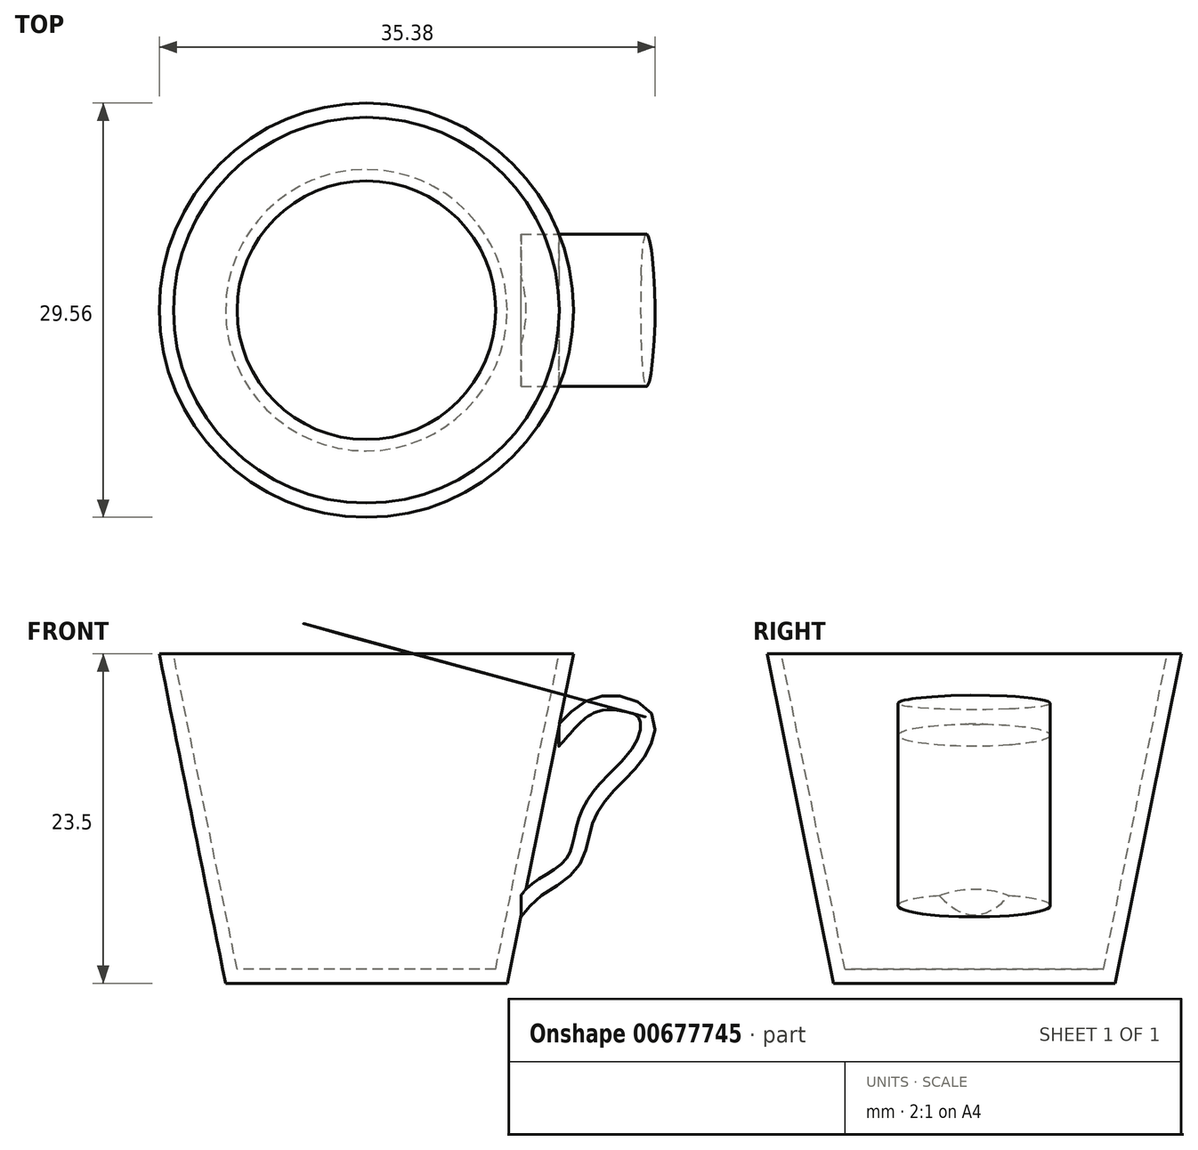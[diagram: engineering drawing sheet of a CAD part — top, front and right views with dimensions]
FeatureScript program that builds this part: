
annotation { "Feature Type Name" : "Feature", "Feature Type Description" : "" }
export const myFeature = defineFeature(function(context is Context, id is Id, definition is map)
    precondition{}
    {
        {
            var Q0;
            Q0=qCreatedBy(makeId("Front.planeOp"),FACE);
            var sketch = newSketch(context, id + "F0", { "sketchPlane" : qUnion([Q0])});
            skLineSegment(sketch, "E0", {"start": v(45.77, 48.7) * mm, "end": v(60.56, 48.7) * mm});
            skLineSegment(sketch, "E1", {"start": v(60.56, 48.7) * mm, "end": v(55.82, 25.2) * mm});
            skLineSegment(sketch, "E2", {"start": v(55.82, 25.2) * mm, "end": v(45.77, 25.2) * mm});
            skLineSegment(sketch, "E3", {"start": v(45.77, 25.2) * mm, "end": v(45.77, 48.7) * mm});
            skPoint(sketch, "E4.5.internal.snap0", {"position": v(58.19, 36.96) * mm});
            skPoint(sketch, "E4.7.internal.snap0", {"position": v(58.19, 36.96) * mm});
            skFitSpline(sketch, "E4", {"points": [v(59.42, 43.06) * mm, v(62.45, 45.3) * mm, v(65.67, 44.35) * mm, v(65.48, 41.89) * mm, v(63.4, 39.42) * mm, v(61.7, 36.96) * mm, v(60.56, 33.74) * mm, v(58.19, 31.84) * mm, v(56.9, 30.6) * mm], "startDerivative": vector(19.06, 21.07) * mm, "endDerivative": vector(-11.26, -12.92) * mm});
            skSolve(sketch);
        }
        {
            var Q0;
            Q0=makeQuery(id+"F0.imprint","IMPRINT",FACE,{"disambiguationData":[TD([[makeQuery(id+"F0.imprint","IMPRINT",EDGE,{"derivedFrom":sQuery(id+"F0.wireOp",EDGE,"E0")}),-1.0]])]});
            var Q1;
            Q1=sQuery(id+"F0.wireOp",EDGE,"E3");
            revolve(context, id + "F1", {"entities" : qUnion([Q0]), "axis" : qUnion([Q1]), "revolveType" : RevolveType.FULL});
        }
        {
            var Q0;
            Q0=makeQuery(id+"F1.opRevolve","SWEPT_FACE",FACE,{"disambiguationData":[OSD([sQuery(id+"F0.wireOp",EDGE,"E0")])]});
            shell(context, id + "F2", {"entities" : qUnion([Q0]), "thickness" : 1 * mm});
        }
        {
            var Q0;
            Q0=qCreatedBy(makeId("Right.planeOp"),FACE);
            cPlane(context, id + "F3", {"entities" : qUnion([Q0]), "cplaneType" : CPlaneType.OFFSET, "offset" : 56.8 * mm, "width" : 150 * mm, "height" : 150 * mm});
        }
        {
            var Q0;
            Q0=qCreatedBy(id+"F3.planeOp",FACE);
            var sketch = newSketch(context, id + "F4", { "sketchPlane" : qUnion([Q0])});
            skEllipse(sketch, "E5", {"center": v(34.14, 16.53) * mm, "majorRadius": 11.6 * mm, "minorRadius": 2.6 * mm, "majorAxis": v(1, 0)});
            skEllipse(sketch, "E6", {"center": v(0, 30.75) * mm, "majorRadius": 5.43 * mm, "minorRadius": 0.8 * mm, "majorAxis": v(1, 0)});
            skSolve(sketch);
        }
        {
            var Q0;
            Q0=makeQuery(id+"F4.imprint","IMPRINT",FACE,{"disambiguationData":[TD([[makeQuery(id+"F4.imprint","IMPRINT",EDGE,{"derivedFrom":sQuery(id+"F4.wireOp",EDGE,"E6")}),1.0]])]});
            var Q1;
            Q1=sQuery(id+"F0.wireOp",EDGE,"E4");
            sweep(context, id + "F5", {"operationType" : NewBodyOperationType.ADD, "profiles" : qUnion([Q0]), "path" : qUnion([Q1])});
        }
    });
